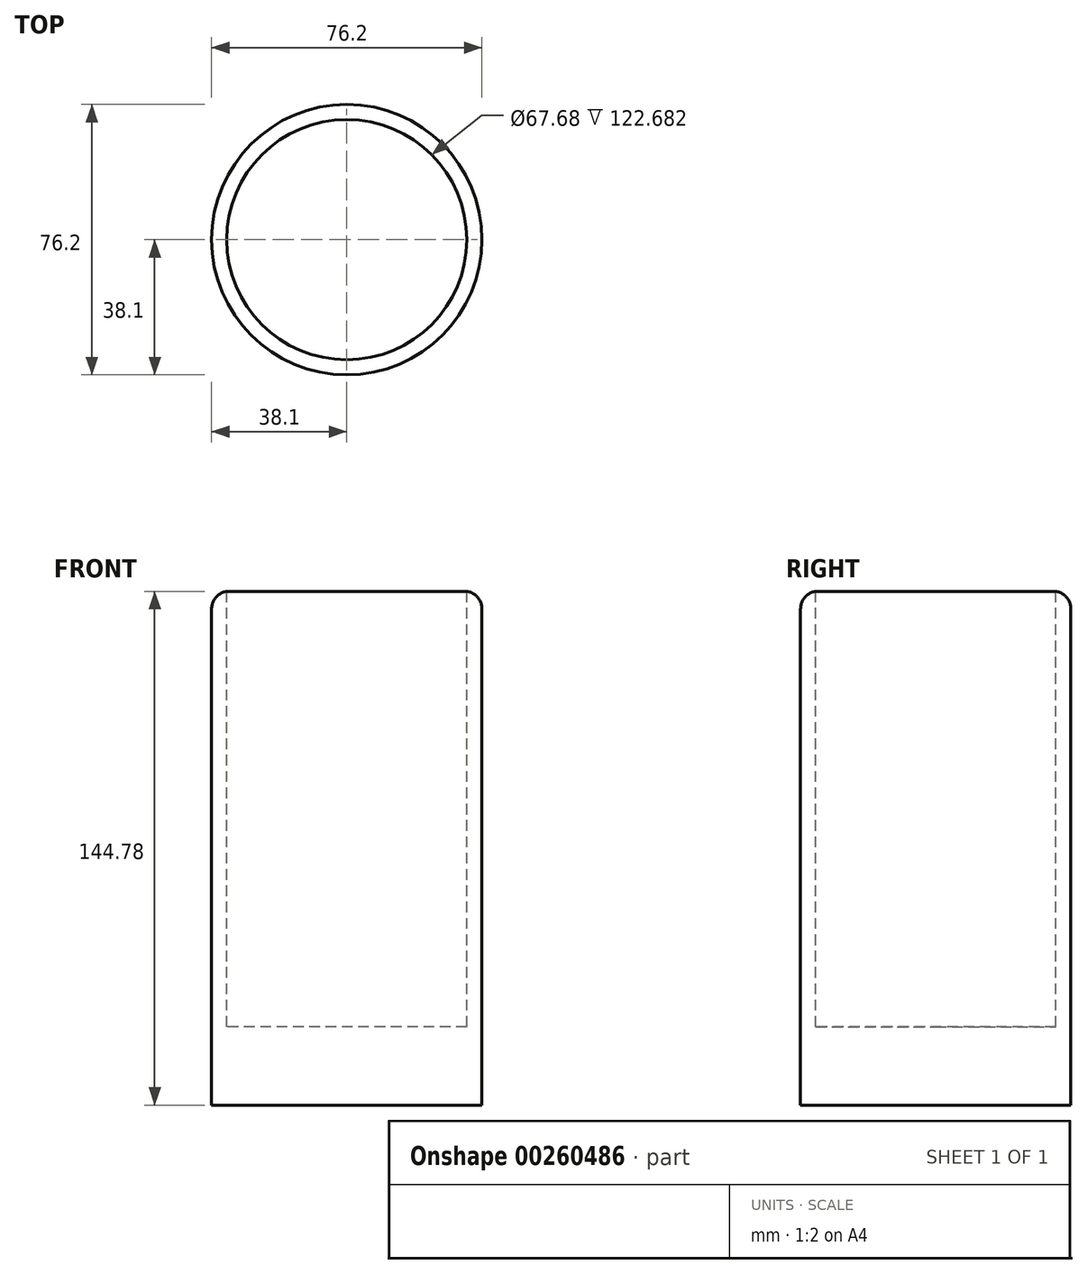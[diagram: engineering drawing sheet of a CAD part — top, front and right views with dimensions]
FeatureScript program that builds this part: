
annotation { "Feature Type Name" : "Feature", "Feature Type Description" : "" }
export const myFeature = defineFeature(function(context is Context, id is Id, definition is map)
    precondition{}
    {
        {
            var Q0;
            Q0=qCreatedBy(makeId("Top.planeOp"),FACE);
            var sketch = newSketch(context, id + "F0", { "sketchPlane" : qUnion([Q0])});
            skCircle(sketch, "E0", {"center": v(0, 0) * mm, "radius": 38.1 * mm});
            skSolve(sketch);
        }
        {
            var Q0;
            Q0 = qSketchRegion(id + "F0", true);
            extrude(context, id + "F1", {"entities" : qUnion([Q0]), "depth" : 20.32 * mm});
        }
        {
            var Q0;
            Q0=makeQuery(id+"F1.opExtrude","CAP_FACE",FACE,{"disambiguationData":[OSD([sQuery(id+"F0.wireOp",EDGE,"E0")])],"isStart":false});
            var sketch = newSketch(context, id + "F2", { "sketchPlane" : qUnion([Q0])});
            skCircle(sketch, "E1", {"center": v(0, 0) * mm, "radius": 38.1 * mm});
            skSolve(sketch);
        }
        {
            var Q0;
            Q0=makeQuery(id+"F2.imprint","IMPRINT",FACE,{"disambiguationData":[TD([[makeQuery(id+"F2.imprint","IMPRINT",EDGE,{"derivedFrom":sQuery(id+"F2.wireOp",EDGE,"E1")}),1.0]])]});
            extrude(context, id + "F3", {"entities" : qUnion([Q0]), "operationType" : NewBodyOperationType.ADD, "depth" : 124.46 * mm});
        }
        {
            var Q0;
            Q0=makeQuery(id+"F3.opExtrude","CAP_FACE",FACE,{"disambiguationData":[OSD([sQuery(id+"F2.wireOp",EDGE,"E1")])],"isStart":false});
            var sketch = newSketch(context, id + "F4", { "sketchPlane" : qUnion([Q0])});
            skLineSegment(sketch, "E2", {"start": v(-38.1, 0) * mm, "end": v(-31.7, 0) * mm});
            skCircle(sketch, "E3", {"center": v(0, 0) * mm, "radius": 33.84 * mm});
            skSolve(sketch);
        }
        {
            var Q0;
            Q0 = qSketchRegion(id + "F4", true);
            var Q1;
            Q1=makeQuery(id+"F4.imprint","IMPRINT",FACE,{"disambiguationData":[TD([[makeQuery(id+"F4.imprint","IMPRINT",EDGE,{"derivedFrom":sQuery(id+"F4.wireOp",EDGE,"KQwPNkJB-Z3De-YCN3-YDQ0-yd12cKxgNXsm")}),1.0]])]});
            extrude(context, id + "F5", {"entities" : qUnion([Q0, Q1]), "operationType" : NewBodyOperationType.REMOVE, "endBound" : BoundingType.SYMMETRIC, "oppositeDirection" : true, "depth" : 245.36 * mm});
        }
        {
            var Q0;
            Q0=makeQuery(id+"F3.opExtrude","CAP_EDGE",EDGE,{"disambiguationData":[OSD([sQuery(id+"F2.wireOp",EDGE,"E1")])],"isStart":false});
            fillet(context, id + "F6", {"entities" : qUnion([Q0]), "radius" : 5.08 * mm, "tangentPropagation" : true, "allowEdgeOverflow" : false});
        }
    });
